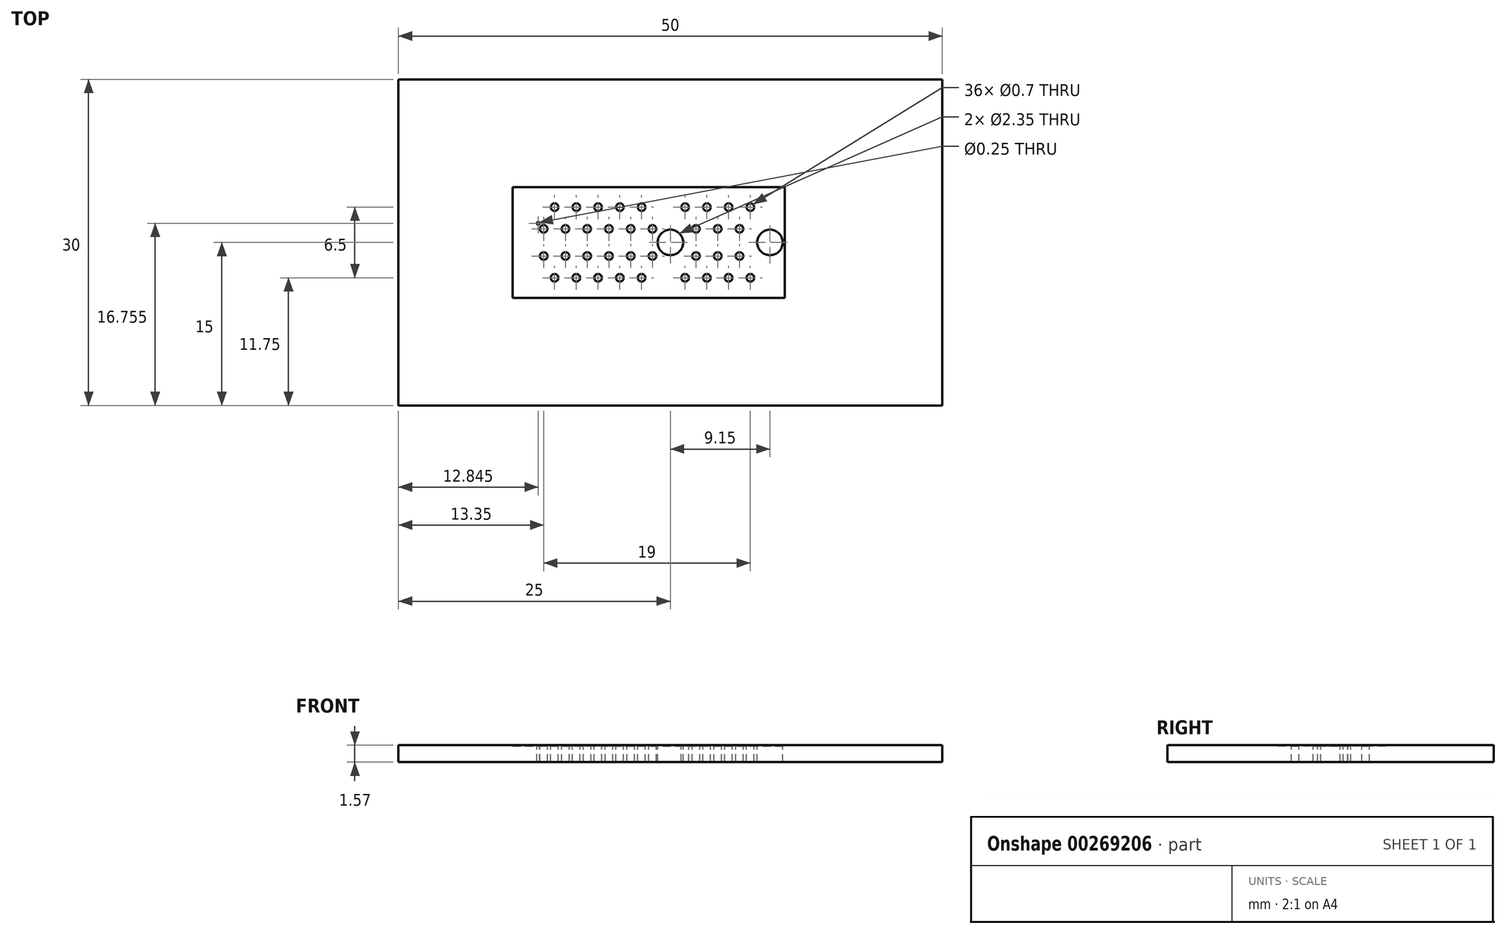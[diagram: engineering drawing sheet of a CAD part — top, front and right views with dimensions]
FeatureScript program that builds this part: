
annotation { "Feature Type Name" : "Feature", "Feature Type Description" : "" }
export const myFeature = defineFeature(function(context is Context, id is Id, definition is map)
    precondition{}
    {
        {
            var Q0;
            Q0=qCreatedBy(makeId("Top.planeOp"),FACE);
            var sketch = newSketch(context, id + "F0", { "sketchPlane" : qUnion([Q0])});
            skLineSegment(sketch, "E0.bottom", {"start": v(25, 15) * mm, "end": v(-25, 15) * mm});
            skLineSegment(sketch, "E0.top", {"start": v(25, -15) * mm, "end": v(-25, -15) * mm});
            skLineSegment(sketch, "E0.left", {"start": v(25, 15) * mm, "end": v(25, -15) * mm});
            skLineSegment(sketch, "E0.right", {"start": v(-25, 15) * mm, "end": v(-25, -15) * mm});
            skPoint(sketch, "E0.middle", {"position": v(0, 0) * mm});
            skSolve(sketch);
        }
        {
            var Q0;
            Q0 = qSketchRegion(id + "F0", true);
            extrude(context, id + "F1", {"entities" : qUnion([Q0]), "depth" : 1.57 * mm});
        }
        {
            var Q0;
            Q0=makeQuery(id+"F1.opExtrude","CAP_FACE",FACE,{"disambiguationData":[OSD([sQuery(id+"F0.wireOp",EDGE,"E0.bottom"),sQuery(id+"F0.wireOp",EDGE,"E0.top"),sQuery(id+"F0.wireOp",EDGE,"E0.left"),sQuery(id+"F0.wireOp",EDGE,"E0.right")])],"isStart":false});
            var sketch = newSketch(context, id + "F2", { "sketchPlane" : qUnion([Q0])});
            skCircle(sketch, "E1", {"center": v(0, 0) * mm, "radius": 1.18 * mm});
            skCircle(sketch, "E2", {"center": v(9.15, 0) * mm, "radius": 1.18 * mm});
            skCircle(sketch, "E3", {"center": v(-1.65, 1.25) * mm, "radius": 0.35 * mm});
            skCircle(sketch, "E4", {"center": v(-1.65, -1.25) * mm, "radius": 0.35 * mm});
            skCircle(sketch, "E5", {"center": v(1.35, 3.25) * mm, "radius": 0.35 * mm});
            skCircle(sketch, "E6", {"center": v(1.35, -3.25) * mm, "radius": 0.35 * mm});
            skCircle(sketch, "E7", {"center": v(-3.65, -1.25) * mm, "radius": 0.35 * mm});
            skCircle(sketch, "E8", {"center": v(-5.65, -1.25) * mm, "radius": 0.35 * mm});
            skCircle(sketch, "E9", {"center": v(-7.65, -1.25) * mm, "radius": 0.35 * mm});
            skCircle(sketch, "E10", {"center": v(-9.65, -1.25) * mm, "radius": 0.35 * mm});
            skCircle(sketch, "E11", {"center": v(-11.65, -1.25) * mm, "radius": 0.35 * mm});
            skCircle(sketch, "E12", {"center": v(-3.65, 1.25) * mm, "radius": 0.35 * mm});
            skCircle(sketch, "E13", {"center": v(-5.65, 1.25) * mm, "radius": 0.35 * mm});
            skCircle(sketch, "E14", {"center": v(-7.65, 1.25) * mm, "radius": 0.35 * mm});
            skCircle(sketch, "E15", {"center": v(-11.65, 1.25) * mm, "radius": 0.35 * mm});
            skCircle(sketch, "E16", {"center": v(-9.65, 1.25) * mm, "radius": 0.35 * mm});
            skCircle(sketch, "E17", {"center": v(-2.65, 3.25) * mm, "radius": 0.35 * mm});
            skCircle(sketch, "E18", {"center": v(-4.65, 3.25) * mm, "radius": 0.35 * mm});
            skCircle(sketch, "E19", {"center": v(-6.65, 3.25) * mm, "radius": 0.35 * mm});
            skCircle(sketch, "E20", {"center": v(-8.65, 3.25) * mm, "radius": 0.35 * mm});
            skCircle(sketch, "E21", {"center": v(-10.65, 3.25) * mm, "radius": 0.35 * mm});
            skCircle(sketch, "E22", {"center": v(-2.65, -3.25) * mm, "radius": 0.35 * mm});
            skCircle(sketch, "E23", {"center": v(-4.65, -3.25) * mm, "radius": 0.35 * mm});
            skCircle(sketch, "E24", {"center": v(-6.65, -3.25) * mm, "radius": 0.35 * mm});
            skCircle(sketch, "E25", {"center": v(-8.65, -3.25) * mm, "radius": 0.35 * mm});
            skCircle(sketch, "E26", {"center": v(-10.65, -3.25) * mm, "radius": 0.35 * mm});
            skCircle(sketch, "E27", {"center": v(3.35, -3.25) * mm, "radius": 0.35 * mm});
            skCircle(sketch, "E28", {"center": v(5.35, -3.25) * mm, "radius": 0.35 * mm});
            skCircle(sketch, "E29", {"center": v(7.35, -3.25) * mm, "radius": 0.35 * mm});
            skCircle(sketch, "E30", {"center": v(3.35, 3.25) * mm, "radius": 0.35 * mm});
            skCircle(sketch, "E31", {"center": v(5.35, 3.25) * mm, "radius": 0.35 * mm});
            skCircle(sketch, "E32", {"center": v(7.35, 3.25) * mm, "radius": 0.35 * mm});
            skCircle(sketch, "E33", {"center": v(2.35, -1.25) * mm, "radius": 0.35 * mm});
            skCircle(sketch, "E34", {"center": v(4.35, -1.25) * mm, "radius": 0.35 * mm});
            skCircle(sketch, "E35", {"center": v(6.35, -1.25) * mm, "radius": 0.35 * mm});
            skCircle(sketch, "E36", {"center": v(2.35, 1.25) * mm, "radius": 0.35 * mm});
            skCircle(sketch, "E37", {"center": v(4.35, 1.25) * mm, "radius": 0.35 * mm});
            skCircle(sketch, "E38", {"center": v(6.35, 1.25) * mm, "radius": 0.35 * mm});
            skCircle(sketch, "E39", {"center": v(-12.15, 1.75) * mm, "radius": 0.12 * mm});
            skLineSegment(sketch, "E40.bottom", {"start": v(-11.65, 1.25) * mm, "end": v(-12.15, 1.25) * mm, "construction": true});
            skLineSegment(sketch, "E40.top", {"start": v(-11.65, 1.75) * mm, "end": v(-12.15, 1.75) * mm, "construction": true});
            skLineSegment(sketch, "E40.left", {"start": v(-11.65, 1.25) * mm, "end": v(-11.65, 1.75) * mm, "construction": true});
            skLineSegment(sketch, "E40.right", {"start": v(-12.15, 1.25) * mm, "end": v(-12.15, 1.75) * mm, "construction": true});
            skSolve(sketch);
        }
        {
            var Q0;
            Q0 = qSketchRegion(id + "F2", true);
            var Q1;
            Q1=sQuery(id+"F2.wireOp",EDGE,"E40.top");
            var Q2;
            Q2=sQuery(id+"F2.wireOp",EDGE,"E40.right");
            var Q3;
            Q3=sQuery(id+"F2.wireOp",EDGE,"E40.bottom");
            var Q4;
            Q4=sQuery(id+"F2.wireOp",EDGE,"E40.left");
            extrude(context, id + "F3", {"entities" : qUnion([Q0]), "operationType" : NewBodyOperationType.REMOVE, "surfaceEntities" : qUnion([Q1, Q2, Q3, Q4]), "oppositeDirection" : true, "depth" : 25 * mm});
        }
        {
            var Q0;
            Q0=makeQuery(id+"F1.opExtrude","CAP_FACE",FACE,{"disambiguationData":[OSD([sQuery(id+"F0.wireOp",EDGE,"E0.bottom"),sQuery(id+"F0.wireOp",EDGE,"E0.top"),sQuery(id+"F0.wireOp",EDGE,"E0.left"),sQuery(id+"F0.wireOp",EDGE,"E0.right")])],"isStart":false});
            var sketch = newSketch(context, id + "F4", { "sketchPlane" : qUnion([Q0])});
            skLineSegment(sketch, "E41.bottom", {"start": v(-14.5, 5.1) * mm, "end": v(10.5, 5.1) * mm});
            skLineSegment(sketch, "E41.top", {"start": v(-14.5, -5.1) * mm, "end": v(10.5, -5.1) * mm});
            skLineSegment(sketch, "E41.left", {"start": v(-14.5, 5.1) * mm, "end": v(-14.5, -5.1) * mm});
            skLineSegment(sketch, "E41.right", {"start": v(10.5, 5.1) * mm, "end": v(10.5, -5.1) * mm});
            skLineSegment(sketch, "E42", {"start": v(-14.5, 0) * mm, "end": v(10.5, 0) * mm, "construction": true});
            skLineSegment(sketch, "E43", {"start": v(0, 5.1) * mm, "end": v(0, -5.1) * mm, "construction": true});
            skPoint(sketch, "E44", {"position": v(-11.65, 1.25) * mm});
            skSolve(sketch);
        }
        {
            var Q0;
            Q0 = qSketchRegion(id + "F4", true);
            extrude(context, id + "F5", {"entities" : qUnion([Q0]), "operationType" : NewBodyOperationType.REMOVE, "oppositeDirection" : true, "depth" : .1 * mm});
        }
    });
